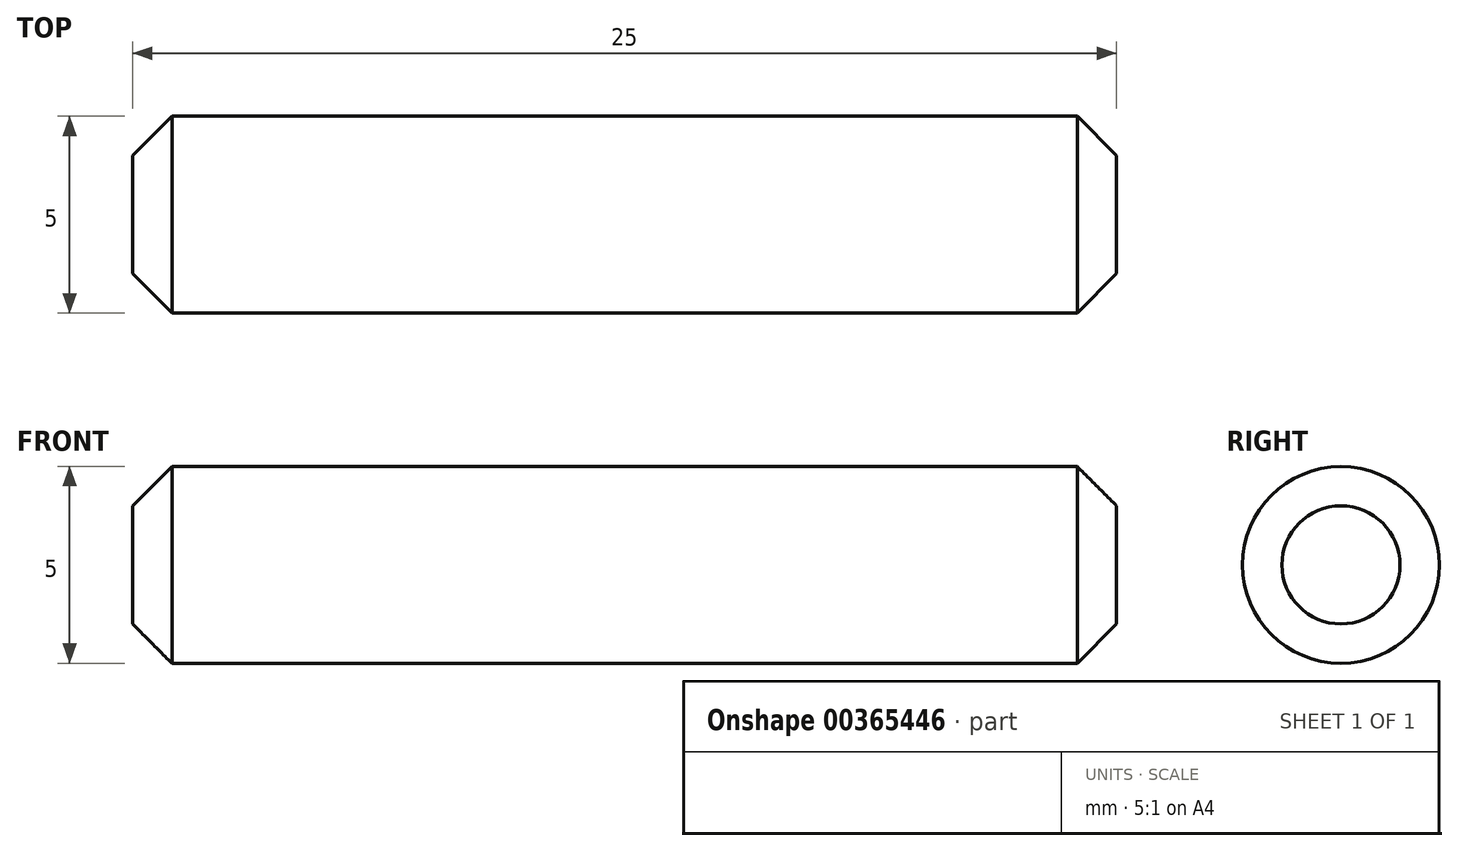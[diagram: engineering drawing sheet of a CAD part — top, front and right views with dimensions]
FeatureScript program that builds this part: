
annotation { "Feature Type Name" : "Feature", "Feature Type Description" : "" }
export const myFeature = defineFeature(function(context is Context, id is Id, definition is map)
    precondition{}
    {
        {
            var Q0;
            Q0=qCreatedBy(makeId("Front.planeOp"),FACE);
            var sketch = newSketch(context, id + "F0", { "sketchPlane" : qUnion([Q0])});
            skLineSegment(sketch, "E0", {"start": v(25, 0) * mm, "end": v(25, 2.5) * mm});
            skLineSegment(sketch, "E1", {"start": v(25, 2.5) * mm, "end": v(0, 2.5) * mm});
            skLineSegment(sketch, "E2", {"start": v(0, 2.5) * mm, "end": v(0, 0) * mm});
            skLineSegment(sketch, "E3", {"start": v(0, 0) * mm, "end": v(25, 0) * mm});
            skSolve(sketch);
        }
        {
            var Q0;
            Q0 = qSketchRegion(id + "F0", true);
            var Q1;
            Q1=sQuery(id+"F0.wireOp",EDGE,"E3");
            revolve(context, id + "F1", {"entities" : qUnion([Q0]), "axis" : qUnion([Q1]), "revolveType" : RevolveType.FULL});
        }
        {
            var Q0;
            Q0=makeQuery(id+"F1.opRevolve","SWEPT_EDGE",EDGE,{"disambiguationData":[OSD([sQuery(id+"F0.wireOp",EDGE,"E0"),sQuery(id+"F0.wireOp",EDGE,"E1")])]});
            var Q1;
            Q1=makeQuery(id+"F1.opRevolve","SWEPT_EDGE",EDGE,{"disambiguationData":[OSD([sQuery(id+"F0.wireOp",EDGE,"E1"),sQuery(id+"F0.wireOp",EDGE,"E2")])]});
            chamfer(context, id + "F2", {"entities" : qUnion([Q0, Q1]), "width" : 1 * mm, "tangentPropagation" : true});
        }
    });
